# Revit family: CWRS
name_source: partatom
category: Lighting Fixtures
units: mm (PartAtom-declared; Revit-internal decimal feet)

## family parameters
Cut with Voids When Loaded = No
Host = Face
Light Source = Yes
OmniClass Number = 23.80.70.11.11
OmniClass Title = General Luminaries, Non Directional
Part Type = Normal
Room Calculation Point = No
Round Connector Dimension = Use Diameter
Shared = No

## types (1)
- CWRS
    Apparent Load = 1 VA
    Application = The CWR remote heads can be applied over path of
egress doors in areas affected by raiin, moisture and
condensation
    Body = Paint - Matte White
    Certification = UL924
    Color Filter = 16777215
    Default Elevation = 48 "
    Description = The CWR remote head can be applied over path of egress doors and in areas affected by rain, moisture and condensation. Includes mounting base and lamp-heads in durable die-cast construction. Lamp-heads are fully gasketed, fully adjustable and glare-free for operation in outdoor and wet environments. The CWR remote lamps are driven exclusively by the Compass CU2W with remote capacity.
    Dimming Lamp Color Temperature Shift = <None>
    Features = Constructed of heavy-duty die-cast with glass lens and
chrome-plated metallized reflector
•	 8 LED’s per head using 1.0W at 9.6 VOLTS DC
•	 LED life-cycle of more than 10 years
•	 Operates from 9.6VDC input from the Compass CU2W
Emergency Light
•	 Lamp base mounts to single-gang switch box
•	 Suitable for wall or ceiling mount
    Glass = Glass - White
    Lamp = LED
    Manufacturer = Compass Products
    Model = CWRS
    Photometric Note = For more photometric file please find the above link
    Photometric Web File = compass_led (1).ies
    Steel = Metal-Galvanized_Steel
    Tilt Angle = 0.00°
    Type Comments = Light Fixture
    URL = https://www.currentlighting.com
    Warranty = 2 year full unit warranty
    Wattage Comments = 1W

## geometry (parser evidence)
native form markers: Sweep x2
no freeform markers — native parametric forms only
